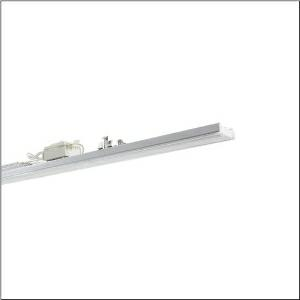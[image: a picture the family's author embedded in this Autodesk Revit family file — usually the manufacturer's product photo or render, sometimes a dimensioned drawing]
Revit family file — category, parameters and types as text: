
# Revit family: licross_21_recessed_ho_52tl12dn4dxm
name_source: partatom
category: Lighting Fixtures
units: mm (PartAtom-declared; Revit-internal decimal feet)

## family parameters
Cut with Voids When Loaded = No
Host = Face
Light Source = No
Part Type = Normal
Room Calculation Point = No
Round Connector Dimension = Use Diameter
Shared = No

## types (1)
- --- (1 x LED, 13000 lm, 72.3 W, 4000K)
    Apparent Load = 72 VA
    CIE Flux Codes = 69 91 98 100 100
    Color Rendering = 80
    Color Temperature = 4000K
    Default Elevation = 1800 mm
    Description = Licross 21 Recessed HO, luminaire insert, of sheet steel, galvanised, coil coated, white, length: 1.500mm, width: 66mm, height: 67mm, LED rated luminous flux: 13.000lm, light colour: 840, SDCM (Standard Deviation of Colour Matching)MacAdam ≤ 3 SDCM (initial), control gear: DALI 2, with plug, 5-pole, with phase selection, mains connection: 220..240V, AC, 50/60Hz, rated input power: 72W, internal wiring halogen-free, primary optical cover: cover, of PMMA, light emission: direct distribution, primary light characteristic: symmetric, protection rating (complete): IP40, insulation class (complete): insulation class I (protective earthing), certification: CE, ENEC, VDE, UKCA, protection symbol: D if used in an environment without relevant dust loads with corresponding accessories, impact resistance: IK06, permissible ambient temperature for indoor applications: -25..+35°C, corresponds to IFS (International Featured Standards) requirements for safety and quality in the food industry, reducing of maximum allowable ambient temperature of 5°C with ceiling mounting, LABS conformity tested according to VDMA 24364:2018-05, The light source and the operating device comply with the requirements of the Ecodesign Regulation (EU) 2019/2020 and are replaceable in accordance with this regulation, packaging unit: 1 piece
    Height = 58 mm
    Lamp = 1 x LED
    Lamp Light Flux = 13000 lm
    Lamp Power = 72.3 W
    Lamp count = 1
    Length = 1500 mm
    Luminous efficacy = 180 lm/W
    Manufacturer = Siteco
    ModVariant = No
    Model = 52TL12DN4DXM
    Mounting Place = Ceiling
    Mounting Type = Pendant
    Number of Poles = 1
    OnlyDefault = Yes
    Power Factor = 1
    Product Name = Licross 21 Recessed HO
    Product group = luminaire insert | ceiling pendant
    ProductGroupID = 901
    Protection Class = Protection class I
    Protection Degree = IP 40
    RLX_Detail_Level = 1
    RLX_Emergency_Light_Flux = 0 lm
    RLX_Emergency_Type = 0
    RLX_Emergency_Type_DB = No
    RlxData = <blob elided: 24885 chars, md5=05398b78>
    Socket = socket
    Standby Power = 0 W
    System Light Flux = 13000 lm
    System Power = 72 W
    Type Comments = factory setting: luminous flux: 100 % | dim-lin: 254 | 414 mA
    Type Image = l_1296930.jpg
    URL = http://relux.com
    VarID = @adj_116643
    Voltage = 0 V
    Weight = 0.00 kg
    Width = 66 mm

## geometry (parser evidence)
native form markers: Blend x4, Sweep x9
no freeform markers — native parametric forms only
